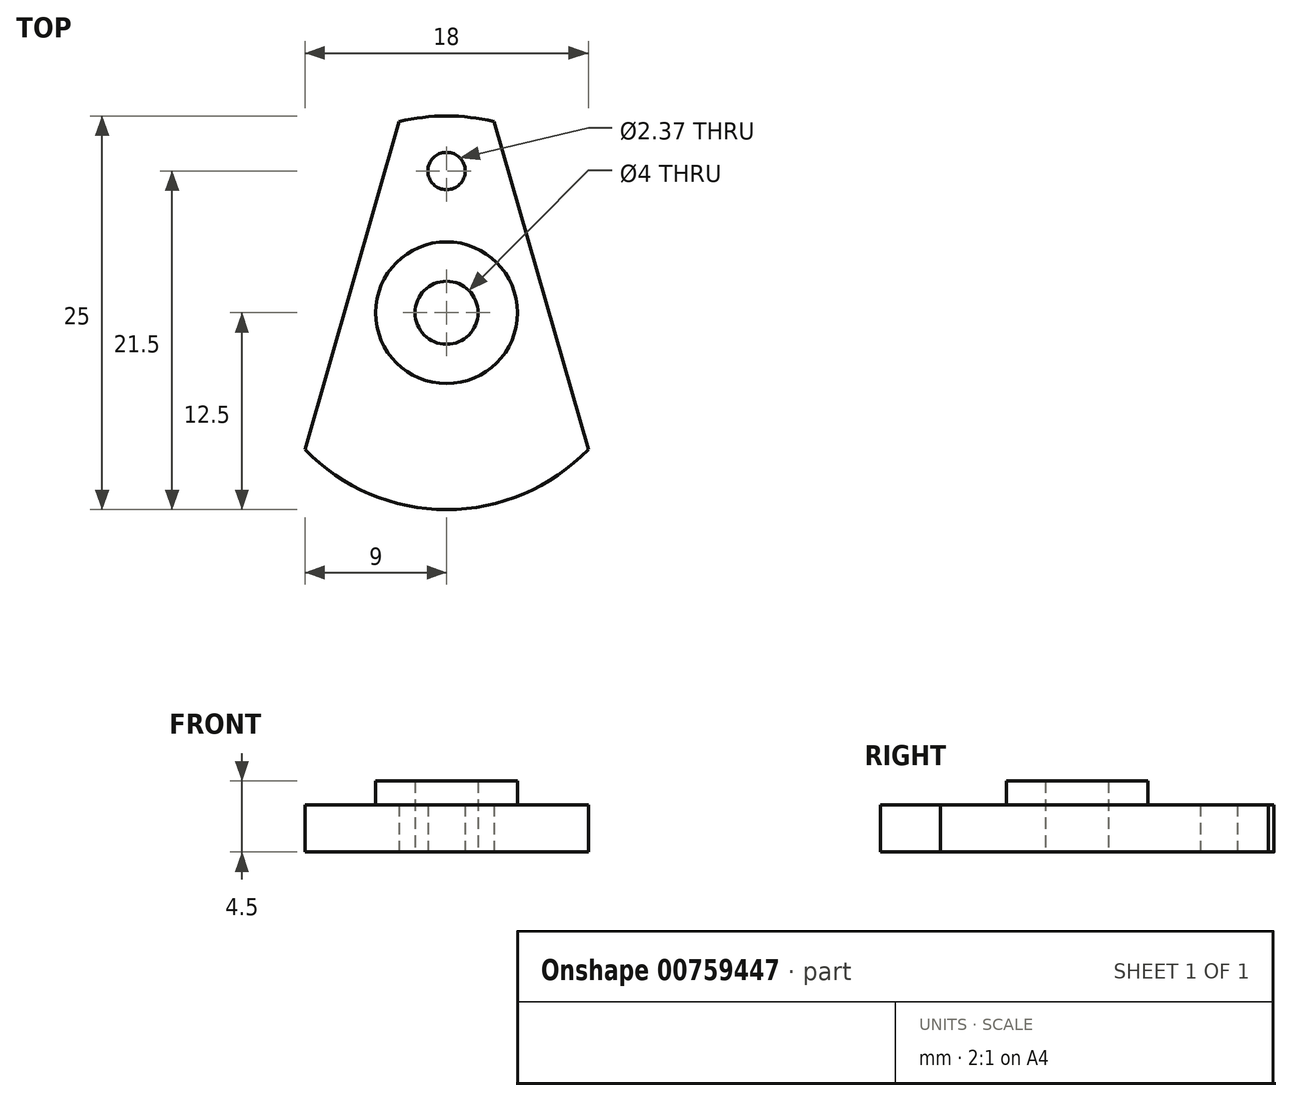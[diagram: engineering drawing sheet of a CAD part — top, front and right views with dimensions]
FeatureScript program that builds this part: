
annotation { "Feature Type Name" : "Feature", "Feature Type Description" : "" }
export const myFeature = defineFeature(function(context is Context, id is Id, definition is map)
    precondition{}
    {
        {
            var Q0;
            Q0=qCreatedBy(makeId("Top.planeOp"),FACE);
            var sketch = newSketch(context, id + "F0", { "sketchPlane" : qUnion([Q0])});
            skArc(sketch, "E0", {"start": v(-9, -8.67) * mm, "mid": v(0, -12.5) * mm, "end": v(9, -8.67) * mm});
            skLineSegment(sketch, "E1", {"start": v(3, 13.95) * mm, "end": v(3, 12.13) * mm, "construction": true});
            skLineSegment(sketch, "E2", {"start": v(3, 12.13) * mm, "end": v(9, -8.67) * mm});
            skLineSegment(sketch, "E3.MirrorCS", {"start": v(-3, 12.13) * mm, "end": v(-9, -8.67) * mm});
            skArc(sketch, "E4.trimOffspring", {"start": v(3, 12.13) * mm, "mid": v(0, 12.5) * mm, "end": v(-3, 12.13) * mm});
            skPoint(sketch, "E5.orphan", {"position": v(9, 13.87) * mm});
            skPoint(sketch, "E6.end.orphan", {"position": v(9, -15.04) * mm});
            skPoint(sketch, "E7.trimOffspring.end.orphan", {"position": v(3, -15.04) * mm});
            skCircle(sketch, "E8", {"center": v(0, 0) * mm, "radius": 4.5 * mm});
            skCircle(sketch, "E9", {"center": v(0, 0) * mm, "radius": 2 * mm});
            skCircle(sketch, "E10", {"center": v(0, 9) * mm, "radius": 1.19 * mm});
            skSolve(sketch);
        }
        {
            var Q0;
            Q0=makeQuery(id+"F0.imprint","IMPRINT",FACE,{"disambiguationData":[TD([[makeQuery(id+"F0.imprint","IMPRINT",EDGE,{"derivedFrom":sQuery(id+"F0.wireOp",EDGE,"E0")}),1.0]])]});
            var Q1;
            Q1=makeQuery(id+"F0.imprint","IMPRINT",FACE,{"disambiguationData":[TD([[makeQuery(id+"F0.imprint","IMPRINT",EDGE,{"derivedFrom":sQuery(id+"F0.wireOp",EDGE,"E8")}),1.0]])]});
            extrude(context, id + "F1", {"entities" : qUnion([Q0, Q1]), "depth" : 3 * mm, "offsetDistance" : 25 * mm});
        }
        {
            var Q0;
            Q0=makeQuery(id+"F0.imprint","IMPRINT",FACE,{"disambiguationData":[TD([[makeQuery(id+"F0.imprint","IMPRINT",EDGE,{"derivedFrom":sQuery(id+"F0.wireOp",EDGE,"E8")}),1.0]])]});
            extrude(context, id + "F2", {"entities" : qUnion([Q0]), "operationType" : NewBodyOperationType.ADD, "depth" : 4.5 * mm, "offsetDistance" : 25 * mm});
        }
    });
